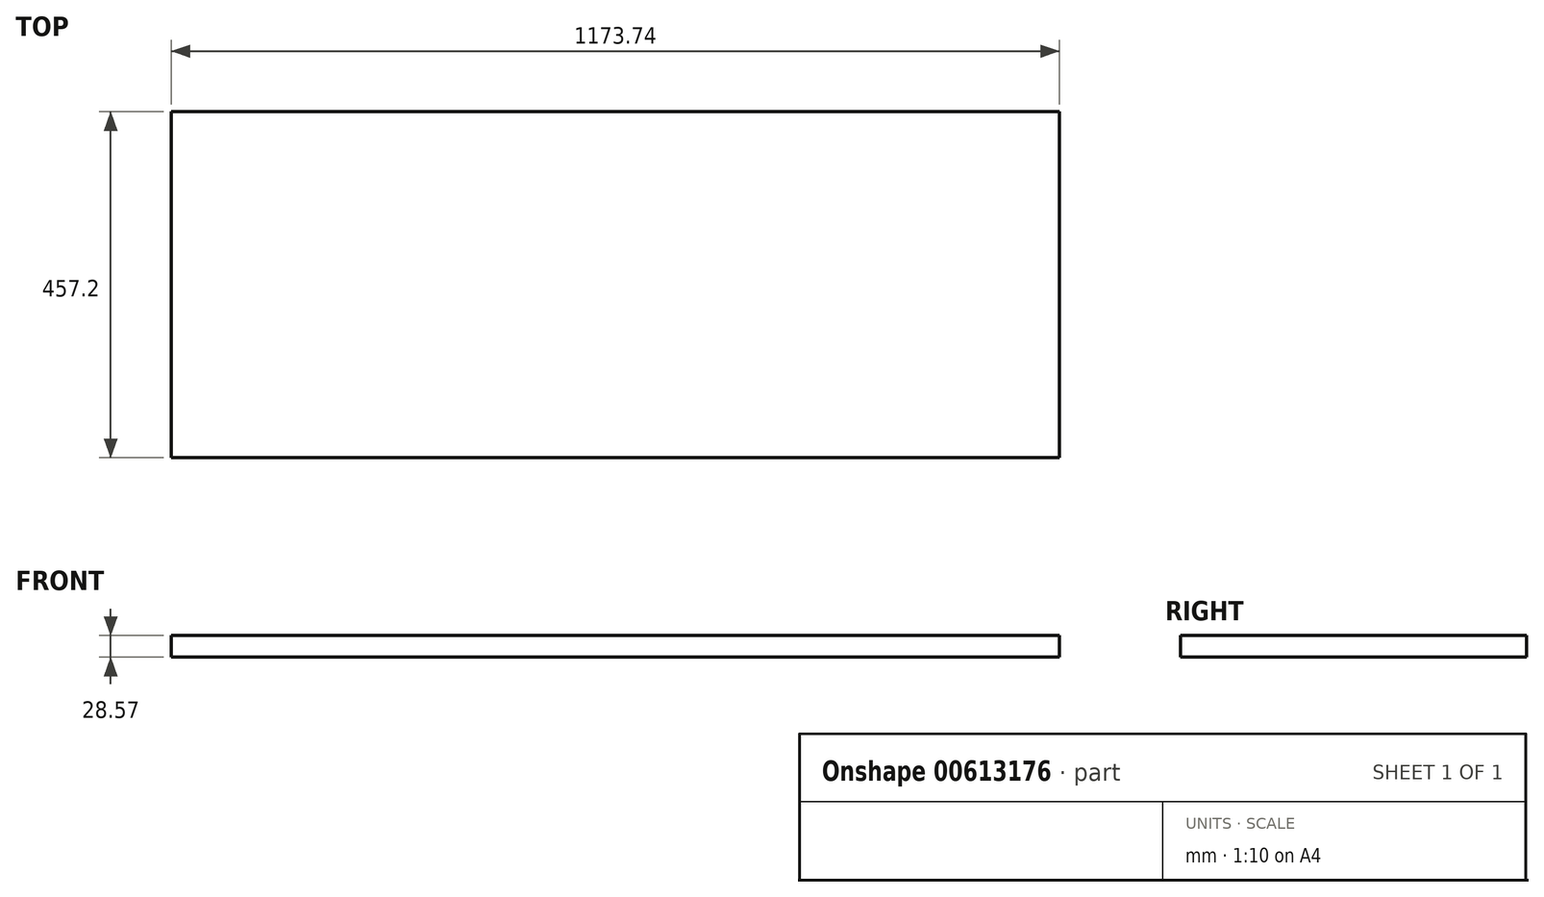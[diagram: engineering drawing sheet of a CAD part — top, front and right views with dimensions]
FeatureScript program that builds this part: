
annotation { "Feature Type Name" : "Feature", "Feature Type Description" : "" }
export const myFeature = defineFeature(function(context is Context, id is Id, definition is map)
    precondition{}
    {
        {
            var Q0;
            Q0=qCreatedBy(makeId("Top.planeOp"),FACE);
            var sketch = newSketch(context, id + "F0", { "sketchPlane" : qUnion([Q0])});
            skLineSegment(sketch, "E0.bottom", {"start": v(586.87, 228.6) * mm, "end": v(-586.87, 228.6) * mm});
            skLineSegment(sketch, "E0.top", {"start": v(586.87, -228.6) * mm, "end": v(-586.87, -228.6) * mm});
            skLineSegment(sketch, "E0.left", {"start": v(586.87, 228.6) * mm, "end": v(586.87, -228.6) * mm});
            skLineSegment(sketch, "E0.right", {"start": v(-586.87, 228.6) * mm, "end": v(-586.87, -228.6) * mm});
            skPoint(sketch, "E0.middle", {"position": v(0, 0) * mm});
            skSolve(sketch);
        }
        {
            var Q0;
            Q0=makeQuery(id+"F0.imprint","IMPRINT",FACE,{"disambiguationData":[TD([[makeQuery(id+"F0.imprint","IMPRINT",EDGE,{"derivedFrom":sQuery(id+"F0.wireOp",EDGE,"E0.bottom")}),1.0]])]});
            extrude(context, id + "F1", {"entities" : qUnion([Q0]), "depth" : 28.57 * mm, "offsetDistance" : 25.4 * mm});
        }
    });
